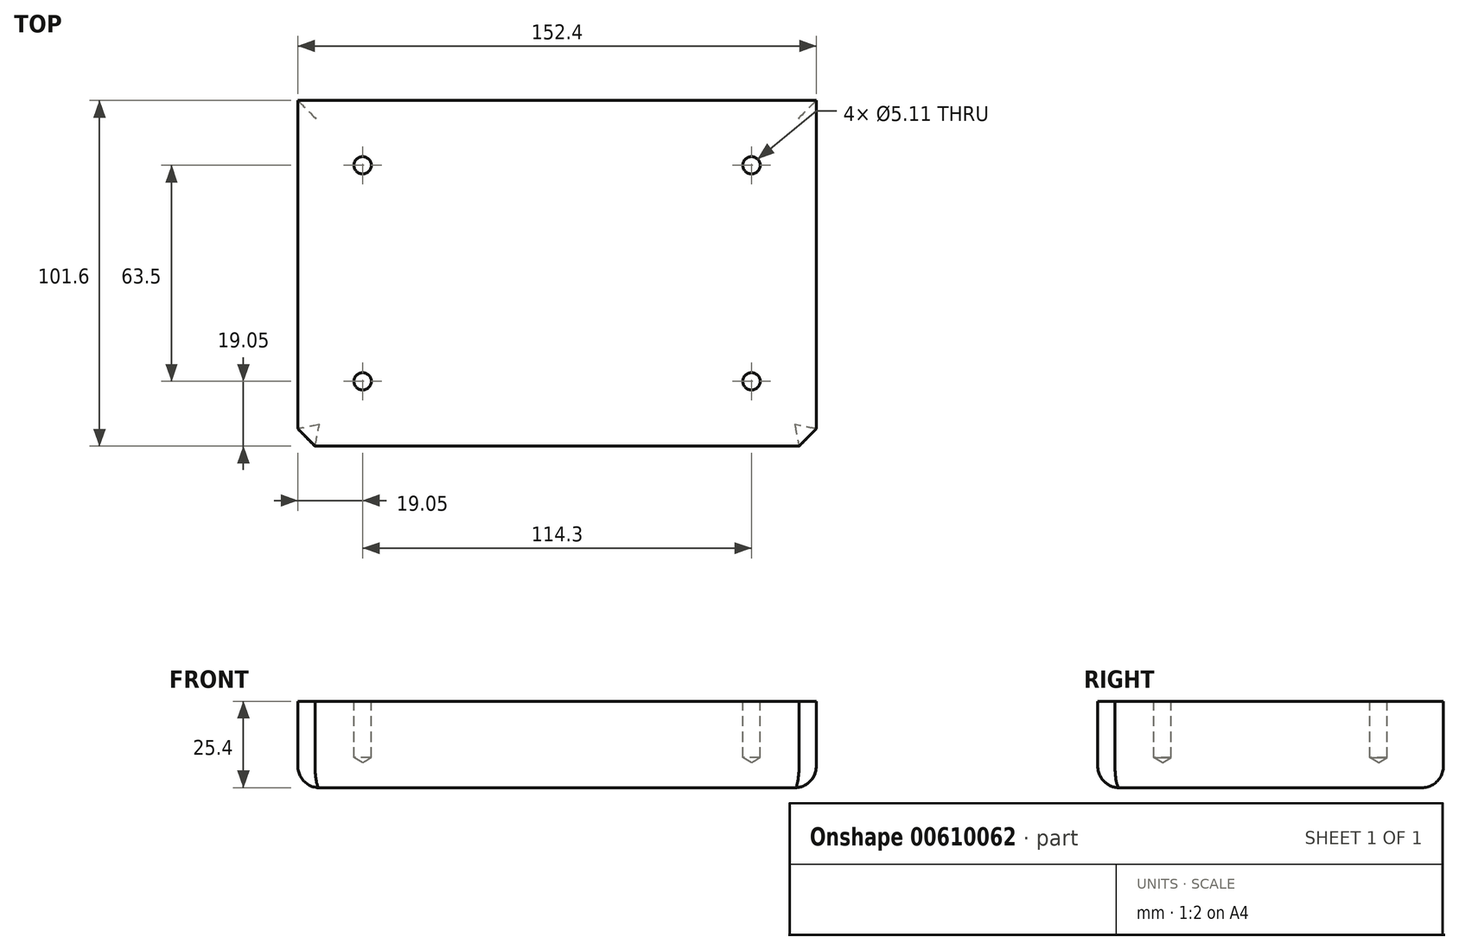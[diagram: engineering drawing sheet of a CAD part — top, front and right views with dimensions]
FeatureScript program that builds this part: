
annotation { "Feature Type Name" : "Feature", "Feature Type Description" : "" }
export const myFeature = defineFeature(function(context is Context, id is Id, definition is map)
    precondition{}
    {
        {
            var Q0;
            Q0=qCreatedBy(makeId("Top.planeOp"),FACE);
            var sketch = newSketch(context, id + "F0", { "sketchPlane" : qUnion([Q0])});
            skLineSegment(sketch, "E0.bottom", {"start": v(-76.2, -50.8) * mm, "end": v(76.2, -50.8) * mm});
            skLineSegment(sketch, "E0.top", {"start": v(-76.2, 50.8) * mm, "end": v(76.2, 50.8) * mm});
            skLineSegment(sketch, "E0.left", {"start": v(-76.2, -50.8) * mm, "end": v(-76.2, 50.8) * mm});
            skLineSegment(sketch, "E0.right", {"start": v(76.2, -50.8) * mm, "end": v(76.2, 50.8) * mm});
            skLineSegment(sketch, "E1", {"start": v(0, 50.8) * mm, "end": v(0, -50.8) * mm, "construction": true});
            skLineSegment(sketch, "E2", {"start": v(76.2, 0) * mm, "end": v(-76.2, 0) * mm, "construction": true});
            skSolve(sketch);
        }
        {
            var Q0;
            Q0=makeQuery(id+"F0.imprint","IMPRINT",FACE,{"disambiguationData":[TD([[makeQuery(id+"F0.imprint","IMPRINT",EDGE,{"derivedFrom":sQuery(id+"F0.wireOp",EDGE,"E0.bottom")}),1.0]])]});
            extrude(context, id + "F1", {"entities" : qUnion([Q0]), "depth" : 25.4 * mm, "offsetDistance" : 25.4 * mm});
        }
        {
            var Q0;
            Q0=makeQuery(id+"F1.opExtrude","CAP_FACE",FACE,{"disambiguationData":[OSD([sQuery(id+"F0.wireOp",EDGE,"E0.bottom"),sQuery(id+"F0.wireOp",EDGE,"E0.top"),sQuery(id+"F0.wireOp",EDGE,"E0.left"),sQuery(id+"F0.wireOp",EDGE,"E0.right")])],"isStart":false});
            var sketch = newSketch(context, id + "F2", { "sketchPlane" : qUnion([Q0])});
            skLineSegment(sketch, "E3.bottom", {"start": v(-57.15, -31.75) * mm, "end": v(57.15, -31.75) * mm, "construction": true});
            skLineSegment(sketch, "E3.top", {"start": v(-57.15, 31.75) * mm, "end": v(57.15, 31.75) * mm, "construction": true});
            skLineSegment(sketch, "E3.left", {"start": v(-57.15, -31.75) * mm, "end": v(-57.15, 31.75) * mm, "construction": true});
            skLineSegment(sketch, "E3.right", {"start": v(57.15, -31.75) * mm, "end": v(57.15, 31.75) * mm, "construction": true});
            skLineSegment(sketch, "E4", {"start": v(0, 31.75) * mm, "end": v(0, 50.8) * mm, "construction": true});
            skLineSegment(sketch, "E5", {"start": v(-57.15, 0) * mm, "end": v(-76.2, 0) * mm, "construction": true});
            skSolve(sketch);
        }
        {
            var Q0;
            Q0=sQuery(id+"F2.wireOp",VERTEX,"E3.left.end");
            var Q1;
            Q1=sQuery(id+"F2.wireOp",VERTEX,"E3.left.start");
            var Q2;
            Q2=sQuery(id+"F2.wireOp",VERTEX,"E3.right.start");
            var Q3;
            Q3=sQuery(id+"F2.wireOp",VERTEX,"E3.top.end");
            var Q4;
            Q4=makeQuery(id+"F1.opExtrude","SWEPT_BODY",BODY,{"disambiguationData":[OSD([sQuery(id+"F0.wireOp",EDGE,"E0.bottom"),sQuery(id+"F0.wireOp",EDGE,"E0.top"),sQuery(id+"F0.wireOp",EDGE,"E0.left"),sQuery(id+"F0.wireOp",EDGE,"E0.right")])]});
            hole(context, id + "F3", {"style" : HoleStyle.SIMPLE, "endStyle" : HoleEndStyle.BLIND, "standardTappedOrClearance" : lookupTablePath({ "standard" : "ANSI", "engagement" : "75%", "pitch" : "20 tpi", "size" : "1/4", "type" : "Tapped" }), "standardBlindInLast" : lookupTablePath({ "standard" : "ANSI", "engagement" : "75%", "pitch" : "20 tpi", "size" : "1/4", "type" : "Tapped" }), "holeDiameter" : 5.1 * mm, "majorDiameter" : 6.35 * mm, "showTappedDepth" : true, "holeDepth" : 16.51 * mm, "tappedDepth" : 12.7 * mm, "tapClearance" : 3, "locations" : qUnion([Q0, Q1, Q2, Q3]), "scope" : qUnion([Q4])});
        }
        {
            var Q0;
            Q0=makeQuery(id+"F1.opExtrude","CAP_FACE",FACE,{"disambiguationData":[OSD([sQuery(id+"F0.wireOp",EDGE,"E0.bottom"),sQuery(id+"F0.wireOp",EDGE,"E0.top"),sQuery(id+"F0.wireOp",EDGE,"E0.left"),sQuery(id+"F0.wireOp",EDGE,"E0.right")])],"isStart":true});
            fillet(context, id + "F4", {"entities" : qUnion([Q0]), "radius" : 6.35 * mm, "tangentPropagation" : true, "allowEdgeOverflow" : false});
        }
        {
            var Q0;
            Q0=makeQuery(id+"F1.opExtrude","SWEPT_EDGE",EDGE,{"disambiguationData":[OSD([sQuery(id+"F0.wireOp",EDGE,"E0.bottom"),sQuery(id+"F0.wireOp",EDGE,"E0.left")])]});
            var Q1;
            Q1=makeQuery(id+"F1.opExtrude","SWEPT_EDGE",EDGE,{"disambiguationData":[OSD([sQuery(id+"F0.wireOp",EDGE,"E0.bottom"),sQuery(id+"F0.wireOp",EDGE,"E0.right")])]});
            chamfer(context, id + "F5", {"entities" : qUnion([Q0, Q1]), "width" : 5.08 * mm, "tangentPropagation" : true});
        }
    });
